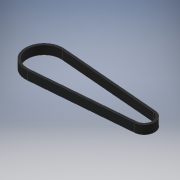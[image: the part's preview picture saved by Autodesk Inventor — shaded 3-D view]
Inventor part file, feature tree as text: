
AUTODESK INVENTOR PART (.ipt)
format: ipt  version: 2018 (Build 220112000, 112)  size: 110,080 bytes
history: native  units: mm
features: extrude x1, sketch x1
ambient origin geometry x8: Origin, YZ Plane, XZ Plane, XY Plane, X Axis, Y Axis, Z Axis, Center Point
bodies: Solido1 (feature_tree)
feature tree (2):
  extrude  "Estrusione1"  Depth=100.0mm
  sketch  "Schizzo1"
